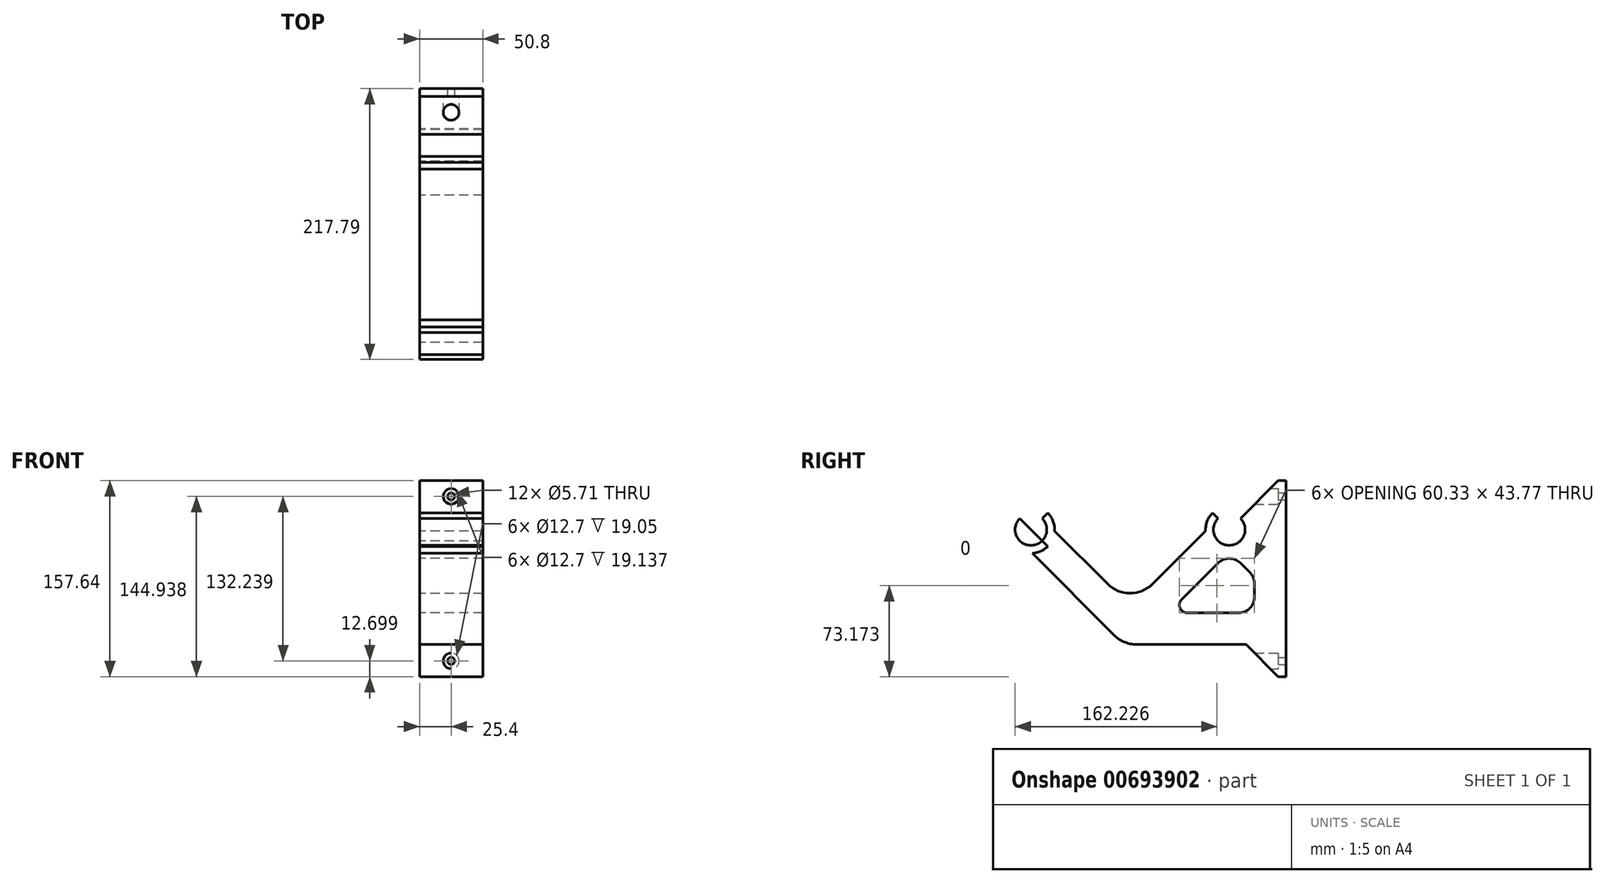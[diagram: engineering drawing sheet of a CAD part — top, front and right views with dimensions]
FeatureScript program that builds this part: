
annotation { "Feature Type Name" : "Feature", "Feature Type Description" : "" }
export const myFeature = defineFeature(function(context is Context, id is Id, definition is map)
    precondition{}
    {
        {
            var Q0;
            Q0=qCreatedBy(makeId("Right.planeOp"),FACE);
            var sketch = newSketch(context, id + "F0", { "sketchPlane" : qUnion([Q0])});
            skCircle(sketch, "E0", {"center": v(0, 0) * mm, "radius": 100 * mm});
            skLineSegment(sketch, "E1", {"start": v(0, 0) * mm, "end": v(0, -100) * mm});
            skLineSegment(sketch, "E2", {"start": v(0, 0) * mm, "end": v(70.71, -70.71) * mm});
            skLineSegment(sketch, "E3.MirrorCS", {"start": v(0, 0) * mm, "end": v(-70.71, -70.71) * mm});
            skCircle(sketch, "E4", {"center": v(79.7, -79.7) * mm, "radius": 12.7 * mm});
            skLineSegment(sketch, "E5", {"start": v(79.7, -79.7) * mm, "end": v(79.7, -67) * mm});
            skLineSegment(sketch, "E6", {"start": v(79.7, -79.7) * mm, "end": v(70.71, -70.71) * mm});
            skCircle(sketch, "E7.MirrorC", {"center": v(-79.7, -79.7) * mm, "radius": 12.7 * mm});
            skLineSegment(sketch, "E8", {"start": v(-79.7, -79.7) * mm, "end": v(-79.7, -67) * mm});
            skLineSegment(sketch, "E9", {"start": v(-79.7, -79.7) * mm, "end": v(-93.16, -66.22) * mm});
            skLineSegment(sketch, "E10.MirrorCS", {"start": v(-79.7, -79.7) * mm, "end": v(-66.22, -66.22) * mm});
            skLineSegment(sketch, "E11.MirrorCS", {"start": v(79.7, -79.7) * mm, "end": v(66.22, -66.22) * mm});
            skLineSegment(sketch, "E12.MirrorCS", {"start": v(79.7, -79.7) * mm, "end": v(93.16, -66.22) * mm});
            skArc(sketch, "E13.trimOffspring", {"start": v(-79.7, -60.64) * mm, "mid": v(-79.6, -60.64) * mm, "end": v(-79.51, -60.64) * mm});
            skLineSegment(sketch, "E14", {"start": v(93.16, -66.22) * mm, "end": v(125.4, -66.22) * mm});
            skPoint(sketch, "E15", {"position": v(100, 0) * mm});
            skCircle(sketch, "E16", {"center": v(79.7, -79.7) * mm, "radius": 19.05 * mm});
            skCircle(sketch, "E17", {"center": v(-79.7, -79.7) * mm, "radius": 19.05 * mm});
            skLineSegment(sketch, "E18", {"start": v(-79.7, -79.7) * mm, "end": v(0, -159.38) * mm});
            skLineSegment(sketch, "E19", {"start": v(79.7, -79.7) * mm, "end": v(0, -159.38) * mm});
            skLineSegment(sketch, "E20", {"start": v(0, -159.38) * mm, "end": v(100, -159.38) * mm});
            skLineSegment(sketch, "E21.1", {"start": v(5.26, -172.08) * mm, "end": v(125.4, -172.08) * mm});
            skLineSegment(sketch, "E21.2", {"start": v(-88.67, -88.67) * mm, "end": v(-12.7, -164.64) * mm});
            skLineSegment(sketch, "E22.0", {"start": v(-70.71, -70.71) * mm, "end": v(-17.96, -123.46) * mm});
            skLineSegment(sketch, "E22.1", {"start": v(46, -146.68) * mm, "end": v(87.3, -146.68) * mm});
            skLineSegment(sketch, "E23.0", {"start": v(70.71, -70.71) * mm, "end": v(17.96, -123.46) * mm});
            skLineSegment(sketch, "E24.0", {"start": v(70.71, -106.63) * mm, "end": v(41.5, -135.84) * mm});
            skPoint(sketch, "E25.visualSharp", {"position": v(0, -141.42) * mm});
            skArc(sketch, "E25.filletArc", {"start": v(-17.96, -123.46) * mm, "mid": v(0, -130.9) * mm, "end": v(17.96, -123.46) * mm});
            skPoint(sketch, "E26.visualSharp", {"position": v(-5.26, -172.08) * mm});
            skArc(sketch, "E26.filletArc", {"start": v(-12.7, -164.64) * mm, "mid": v(-4.46, -170.15) * mm, "end": v(5.26, -172.08) * mm});
            skLineSegment(sketch, "E27", {"start": v(125.4, -66.22) * mm, "end": v(125.4, -172.08) * mm});
            skPoint(sketch, "E28.orphan", {"position": v(92.4, -172.08) * mm});
            skLineSegment(sketch, "E29.0", {"start": v(100, -123.22) * mm, "end": v(100, -133.98) * mm});
            skLineSegment(sketch, "E30", {"start": v(79.7, -79.7) * mm, "end": v(100, -100) * mm});
            skLineSegment(sketch, "E31.0", {"start": v(88.67, -106.63) * mm, "end": v(96.28, -114.24) * mm});
            skArc(sketch, "E32.filletArc", {"start": v(88.67, -106.63) * mm, "mid": v(79.7, -102.91) * mm, "end": v(70.71, -106.63) * mm});
            skArc(sketch, "E33.filletArc", {"start": v(100, -123.22) * mm, "mid": v(99.03, -118.36) * mm, "end": v(96.28, -114.24) * mm});
            skArc(sketch, "E34.filletArc", {"start": v(87.3, -146.68) * mm, "mid": v(96.28, -142.96) * mm, "end": v(100, -133.98) * mm});
            skPoint(sketch, "E35.visualSharp", {"position": v(30.66, -146.68) * mm});
            skArc(sketch, "E35.filletArc", {"start": v(41.5, -135.84) * mm, "mid": v(40.12, -142.76) * mm, "end": v(46, -146.68) * mm});
            skLineSegment(sketch, "E36", {"start": v(93.16, -66.22) * mm, "end": v(119.05, -40.33) * mm});
            skLineSegment(sketch, "E37", {"start": v(125.4, -40.33) * mm, "end": v(125.4, -66.22) * mm});
            skLineSegment(sketch, "E38", {"start": v(125.4, -40.33) * mm, "end": v(119.05, -40.33) * mm});
            skPoint(sketch, "E39.orphan", {"position": v(125.4, -33.98) * mm});
            skLineSegment(sketch, "E40", {"start": v(125.4, -119.15) * mm, "end": v(99.33, -119.15) * mm});
            skPoint(sketch, "E41.MirrorP", {"position": v(125.4, -204.32) * mm});
            skLineSegment(sketch, "E42.MirrorCS", {"start": v(125.4, -197.97) * mm, "end": v(119.05, -197.97) * mm});
            skLineSegment(sketch, "E43.MirrorCS", {"start": v(125.4, -197.97) * mm, "end": v(125.4, -172.08) * mm});
            skLineSegment(sketch, "E44.MirrorCS", {"start": v(93.16, -172.08) * mm, "end": v(119.05, -197.97) * mm});
            skSolve(sketch);
        }
        {
            var Q0;
            {var subQ1=sQuery(id+"F0.wireOp",EDGE,"E0");var subQ3=sQuery(id+"F0.wireOp",EDGE,"E16");var subQ4=makeQuery(id+"F0.imprint","INTERSECT",VERTEX,{"disambiguationData":[OD(1.0)],"derivedFrom":[subQ1,subQ3]});Q0=makeQuery(id+"F0.imprint","IMPRINT",FACE,{"disambiguationData":[TD([[makeQuery(id+"F0.imprint","IMPRINT",EDGE,{"disambiguationData":[TD([[subQ4,1.0]])],"derivedFrom":subQ3}),1.0]])]});}
            var Q1;
            {var subQ1=sQuery(id+"F0.wireOp",EDGE,"E0");var subQ3=sQuery(id+"F0.wireOp",EDGE,"E17");var subQ4=makeQuery(id+"F0.imprint","INTERSECT",VERTEX,{"disambiguationData":[OD(1.0)],"derivedFrom":[subQ1,subQ3]});Q1=makeQuery(id+"F0.imprint","IMPRINT",FACE,{"disambiguationData":[TD([[makeQuery(id+"F0.imprint","IMPRINT",EDGE,{"disambiguationData":[TD([[subQ4,-1.0]])],"derivedFrom":subQ3}),1.0]])]});}
            var Q2;
            {var subQ0=sQuery(id+"F0.wireOp",EDGE,"E21.2");var subQ1=sQuery(id+"F0.wireOp",EDGE,"E7.MirrorC");var subQ2=makeQuery(id+"F0.imprint","INTERSECT",VERTEX,{"derivedFrom":[subQ1,subQ0]});Q2=makeQuery(id+"F0.imprint","IMPRINT",FACE,{"disambiguationData":[TD([[makeQuery(id+"F0.imprint","IMPRINT",EDGE,{"disambiguationData":[TD([[subQ2,-1.0]])],"derivedFrom":subQ1}),1.0]])]});}
            var Q3;
            {var subQ1=sQuery(id+"F0.wireOp",EDGE,"E0");var subQ3=sQuery(id+"F0.wireOp",EDGE,"E17");var subQ4=makeQuery(id+"F0.imprint","INTERSECT",VERTEX,{"disambiguationData":[OD(1.0)],"derivedFrom":[subQ1,subQ3]});Q3=makeQuery(id+"F0.imprint","IMPRINT",FACE,{"disambiguationData":[TD([[makeQuery(id+"F0.imprint","IMPRINT",EDGE,{"disambiguationData":[TD([[subQ4,1.0]])],"derivedFrom":subQ3}),1.0]])]});}
            var Q4;
            {var subQ3=sQuery(id+"F0.wireOp",EDGE,"E18");var subQ5=sQuery(id+"F0.wireOp",EDGE,"E17");var subQ6=makeQuery(id+"F0.imprint","INTERSECT",VERTEX,{"derivedFrom":[subQ5,subQ3]});Q4=makeQuery(id+"F0.imprint","IMPRINT",FACE,{"disambiguationData":[TD([[makeQuery(id+"F0.imprint","IMPRINT",EDGE,{"disambiguationData":[TD([[subQ6,-1.0]])],"derivedFrom":subQ5}),1.0]])]});}
            var Q5;
            {var subQ0=sQuery(id+"F0.wireOp",EDGE,"E21.2");var subQ1=sQuery(id+"F0.wireOp",EDGE,"E7.MirrorC");var subQ2=makeQuery(id+"F0.imprint","INTERSECT",VERTEX,{"derivedFrom":[subQ1,subQ0]});Q5=makeQuery(id+"F0.imprint","IMPRINT",FACE,{"disambiguationData":[TD([[makeQuery(id+"F0.imprint","IMPRINT",EDGE,{"disambiguationData":[TD([[subQ2,1.0]])],"derivedFrom":subQ1}),1.0]])]});}
            var Q6;
            {var subQ5=sQuery(id+"F0.wireOp",EDGE,"E25.filletArc");Q6=makeQuery(id+"F0.imprint","IMPRINT",FACE,{"disambiguationData":[TD([[makeQuery(id+"F0.imprint","IMPRINT",EDGE,{"derivedFrom":subQ5}),-1.0]])]});}
            var Q7;
            {var subQ5=sQuery(id+"F0.wireOp",EDGE,"E14");Q7=makeQuery(id+"F0.imprint","IMPRINT",FACE,{"disambiguationData":[TD([[makeQuery(id+"F0.imprint","IMPRINT",EDGE,{"derivedFrom":subQ5}),-1.0]])]});}
            var Q8;
            {var subQ1=sQuery(id+"F0.wireOp",EDGE,"E0");var subQ3=sQuery(id+"F0.wireOp",EDGE,"E16");var subQ4=makeQuery(id+"F0.imprint","INTERSECT",VERTEX,{"disambiguationData":[OD(1.0)],"derivedFrom":[subQ1,subQ3]});Q8=makeQuery(id+"F0.imprint","IMPRINT",FACE,{"disambiguationData":[TD([[makeQuery(id+"F0.imprint","IMPRINT",EDGE,{"disambiguationData":[TD([[subQ4,-1.0]])],"derivedFrom":subQ3}),1.0]])]});}
            var Q9;
            {var subQ0=sQuery(id+"F0.wireOp",EDGE,"E23.0");var subQ5=sQuery(id+"F0.wireOp",EDGE,"E16");var subQ6=makeQuery(id+"F0.imprint","INTERSECT",VERTEX,{"derivedFrom":[subQ5,subQ0]});Q9=makeQuery(id+"F0.imprint","IMPRINT",FACE,{"disambiguationData":[TD([[makeQuery(id+"F0.imprint","IMPRINT",EDGE,{"disambiguationData":[TD([[subQ6,-1.0]])],"derivedFrom":subQ5}),1.0]])]});}
            var Q10;
            {var subQ0=sQuery(id+"F0.wireOp",EDGE,"E19");var subQ1=sQuery(id+"F0.wireOp",EDGE,"E4");var subQ2=makeQuery(id+"F0.imprint","INTERSECT",VERTEX,{"derivedFrom":[subQ1,subQ0]});Q10=makeQuery(id+"F0.imprint","IMPRINT",FACE,{"disambiguationData":[TD([[makeQuery(id+"F0.imprint","IMPRINT",EDGE,{"disambiguationData":[TD([[subQ2,-1.0]])],"derivedFrom":subQ1}),-1.0]])]});}
            var Q11;
            {var subQ0=sQuery(id+"F0.wireOp",EDGE,"E12.MirrorCS");var subQ1=sQuery(id+"F0.wireOp",EDGE,"E4");var subQ2=makeQuery(id+"F0.imprint","INTERSECT",VERTEX,{"derivedFrom":[subQ1,subQ0]});Q11=makeQuery(id+"F0.imprint","IMPRINT",FACE,{"disambiguationData":[TD([[makeQuery(id+"F0.imprint","IMPRINT",EDGE,{"disambiguationData":[TD([[subQ2,1.0]])],"derivedFrom":subQ1}),-1.0]])]});}
            var Q12;
            Q12=makeQuery(id+"F0.imprint","IMPRINT",FACE,{"disambiguationData":[TD([[makeQuery(id+"F0.imprint","IMPRINT",EDGE,{"derivedFrom":sQuery(id+"F0.wireOp",EDGE,"E14")}),1.0]])]});
            var Q13;
            Q13=makeQuery(id+"F0.imprint","IMPRINT",FACE,{"disambiguationData":[TD([[makeQuery(id+"F0.imprint","IMPRINT",EDGE,{"derivedFrom":sQuery(id+"F0.wireOp",EDGE,"E42.MirrorCS")}),-1.0]])]});
            extrude(context, id + "F1", {"entities" : qUnion([Q0, Q1, Q2, Q3, Q4, Q5, Q6, Q7, Q8, Q9, Q10, Q11, Q12, Q13]), "depth" : 50.8 * mm, "offsetDistance" : 25.4 * mm});
        }
        {
            var Q0;
            Q0=makeQuery(id+"F1.opExtrude","SWEPT_FACE",FACE,{"disambiguationData":[OSD([sQuery(id+"F0.wireOp",EDGE,"E27"),sQuery(id+"F0.wireOp",EDGE,"E37"),sQuery(id+"F0.wireOp",EDGE,"E43.MirrorCS")])]});
            var sketch = newSketch(context, id + "F2", { "sketchPlane" : qUnion([Q0])});
            skLineSegment(sketch, "E45", {"start": v(0, -119.15) * mm, "end": v(-50.8, -119.15) * mm});
            skCircle(sketch, "E46", {"center": v(-25.4, -185.27) * mm, "radius": 2.86 * mm});
            skPoint(sketch, "E46.centerSnap0", {"position": v(-25.4, -197.97) * mm});
            skCircle(sketch, "E47.MirrorC", {"center": v(-25.4, -53.03) * mm, "radius": 2.86 * mm});
            skSolve(sketch);
        }
        {
            var Q0;
            Q0 = qSketchRegion(id + "F2", true);
            extrude(context, id + "F3", {"entities" : qUnion([Q0]), "operationType" : NewBodyOperationType.REMOVE, "endBound" : BoundingType.THROUGH_ALL, "oppositeDirection" : true, "depth" : 25.4 * mm, "offsetDistance" : 25.4 * mm});
        }
        {
            var Q0;
            Q0=makeQuery(id+"F1.opExtrude","SWEPT_FACE",FACE,{"disambiguationData":[OSD([sQuery(id+"F0.wireOp",EDGE,"E27"),sQuery(id+"F0.wireOp",EDGE,"E37"),sQuery(id+"F0.wireOp",EDGE,"E43.MirrorCS")])]});
            cPlane(context, id + "F4", {"entities" : qUnion([Q0]), "cplaneType" : CPlaneType.OFFSET, "offset" : 6.35 * mm, "oppositeDirection" : true, "width" : 152.4 * mm, "height" : 152.4 * mm});
        }
        {
            var Q0;
            Q0=qCreatedBy(id+"F4.planeOp",FACE);
            var sketch = newSketch(context, id + "F5", { "sketchPlane" : qUnion([Q0])});
            skCircle(sketch, "E48.0", {"center": v(-25.4, -53.03) * mm, "radius": 2.86 * mm});
            skCircle(sketch, "E49.0", {"center": v(-25.4, -185.27) * mm, "radius": 2.86 * mm});
            skCircle(sketch, "E50", {"center": v(-25.4, -53.03) * mm, "radius": 6.35 * mm});
            skCircle(sketch, "E51", {"center": v(-25.4, -185.27) * mm, "radius": 6.35 * mm});
            skSolve(sketch);
        }
        {
            var Q0;
            Q0 = qSketchRegion(id + "F5", true);
            extrude(context, id + "F6", {"entities" : qUnion([Q0]), "operationType" : NewBodyOperationType.REMOVE, "endBound" : BoundingType.THROUGH_ALL, "oppositeDirection" : true, "depth" : 25.4 * mm, "offsetDistance" : 25.4 * mm});
        }
    });
